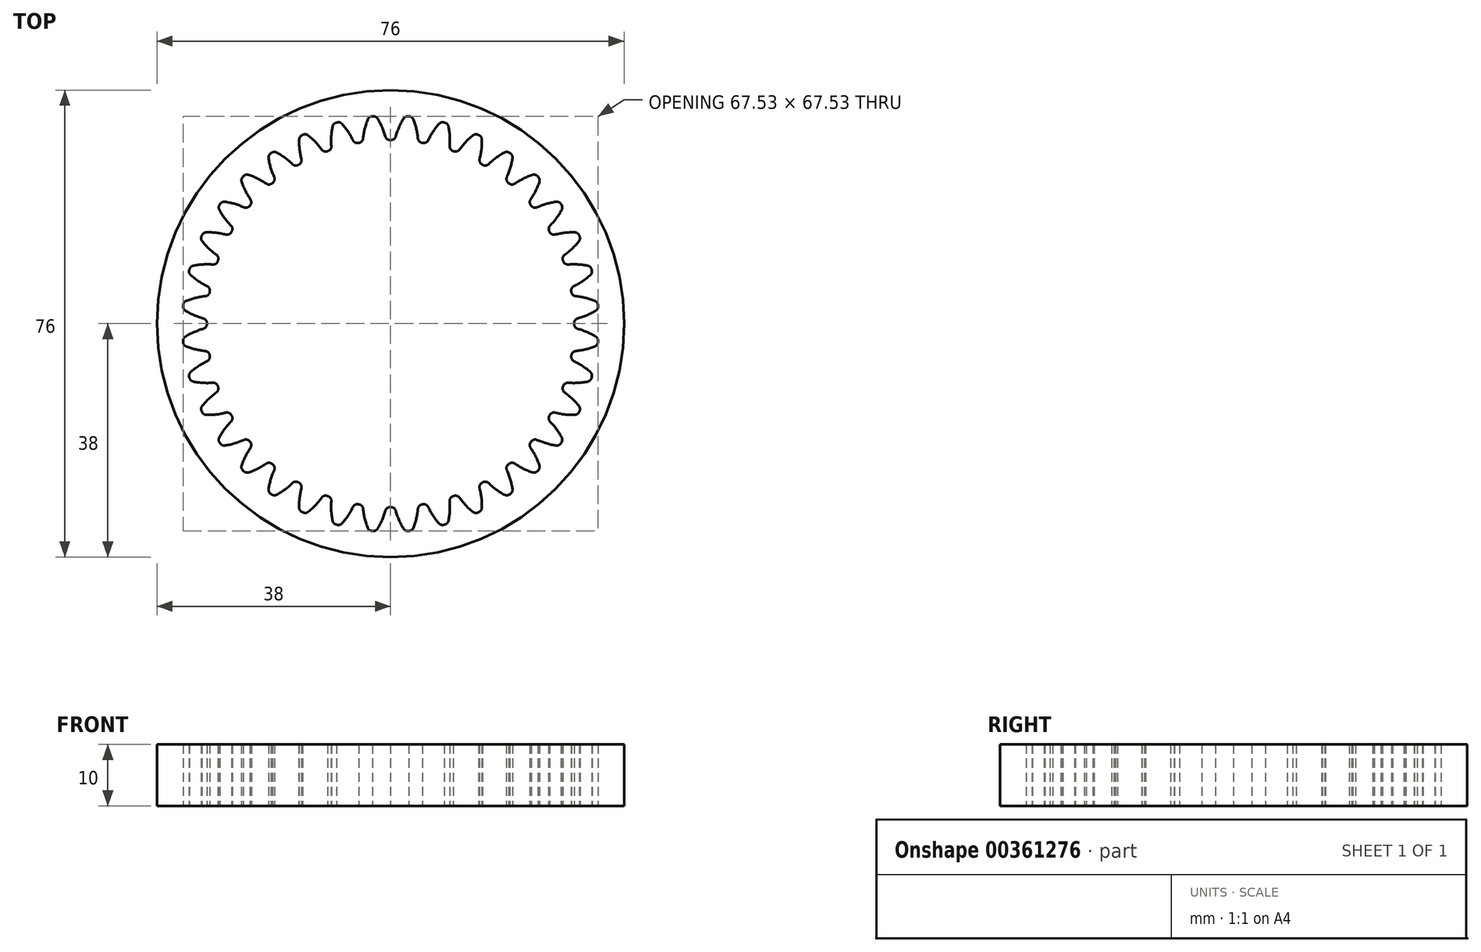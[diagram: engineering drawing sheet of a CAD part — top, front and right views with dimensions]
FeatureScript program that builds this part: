
annotation { "Feature Type Name" : "Feature", "Feature Type Description" : "" }
export const myFeature = defineFeature(function(context is Context, id is Id, definition is map)
    precondition{}
    {
        {
            var Q0;
            Q0=qCreatedBy(makeId("Top.planeOp"),FACE);
            var sketch = newSketch(context, id + "F0", { "sketchPlane" : qUnion([Q0])});
            skCircle(sketch, "E0", {"center": v(0, 0) * mm, "radius": 32.1 * mm, "construction": true});
            skCircle(sketch, "E1", {"center": v(0, 0) * mm, "radius": 33.88 * mm, "construction": true});
            skCircle(sketch, "E2", {"center": v(0, 0) * mm, "radius": 29.88 * mm, "construction": true});
            skLineSegment(sketch, "E3", {"start": v(0, 0) * mm, "end": v(0, 35.03) * mm, "construction": true});
            skLineSegment(sketch, "E4", {"start": v(0, 0) * mm, "end": v(-6.12, 34.73) * mm, "construction": true});
            skLineSegment(sketch, "E5", {"start": v(0, 0) * mm, "end": v(-3.06, 35) * mm, "construction": true});
            skCircle(sketch, "E6", {"center": v(-2.8, 31.98) * mm, "radius": 1.4 * mm, "construction": true});
            skPoint(sketch, "E7.center", {"position": v(0.05, 0.05) * mm});
            skCircle(sketch, "E8", {"center": v(0, 0) * mm, "radius": 38 * mm});
            skCircle(sketch, "E9", {"center": v(-2.8, 31.98) * mm, "radius": 10 * mm, "construction": true});
            skArc(sketch, "E10", {"start": v(-1.92, 21.9) * mm, "mid": v(-1.88, 21.97) * mm, "end": v(-1.85, 22.02) * mm});
            skArc(sketch, "E11.trimOffspring", {"start": v(-0.85, 30.47) * mm, "mid": v(-1.38, 31.97) * mm, "end": v(-2.11, 33.38) * mm});
            skLineSegment(sketch, "E12", {"start": v(-2.85, 33.76) * mm, "end": v(-2.95, 33.76) * mm});
            skLineSegment(sketch, "E13", {"start": v(-0.07, 29.88) * mm, "end": v(0, 29.88) * mm});
            skPoint(sketch, "E14.visualSharp", {"position": v(-0.7, 29.87) * mm});
            skArc(sketch, "E14.filletArc", {"start": v(-0.85, 30.47) * mm, "mid": v(-0.56, 30.04) * mm, "end": v(-0.07, 29.88) * mm});
            skPoint(sketch, "E15.visualSharp", {"position": v(-2.38, 33.8) * mm});
            skArc(sketch, "E15.filletArc", {"start": v(-2.11, 33.38) * mm, "mid": v(-2.43, 33.68) * mm, "end": v(-2.85, 33.76) * mm});
            skArc(sketch, "E16.MirrorCS", {"start": v(-4.46, 30.15) * mm, "mid": v(-4.67, 29.68) * mm, "end": v(-5.12, 29.44) * mm});
            skLineSegment(sketch, "E17.MirrorCS", {"start": v(-5.12, 29.44) * mm, "end": v(-5.19, 29.43) * mm});
            skArc(sketch, "E18.MirrorCS", {"start": v(-4.46, 30.15) * mm, "mid": v(-4.2, 31.72) * mm, "end": v(-3.72, 33.24) * mm});
            skArc(sketch, "E19.MirrorCS", {"start": v(-3.72, 33.24) * mm, "mid": v(-3.46, 33.59) * mm, "end": v(-3.06, 33.75) * mm});
            skLineSegment(sketch, "E20.MirrorCS", {"start": v(-3.06, 33.75) * mm, "end": v(-2.95, 33.76) * mm});
            skArc(sketch, "E21.1.0", {"start": v(-6.12, 29.86) * mm, "mid": v(-5.76, 29.49) * mm, "end": v(-5.25, 29.41) * mm});
            skLineSegment(sketch, "E21.1.1", {"start": v(-5.25, 29.41) * mm, "end": v(-5.19, 29.43) * mm});
            skArc(sketch, "E21.1.2", {"start": v(-6.12, 29.86) * mm, "mid": v(-6.9, 31.25) * mm, "end": v(-7.88, 32.51) * mm});
            skArc(sketch, "E21.1.3", {"start": v(-7.88, 32.51) * mm, "mid": v(-8.24, 32.74) * mm, "end": v(-8.67, 32.76) * mm});
            skLineSegment(sketch, "E21.1.4", {"start": v(-8.67, 32.76) * mm, "end": v(-8.77, 32.73) * mm});
            skLineSegment(sketch, "E21.1.5", {"start": v(-8.87, 32.7) * mm, "end": v(-8.77, 32.73) * mm});
            skArc(sketch, "E21.1.6", {"start": v(-9.43, 32.1) * mm, "mid": v(-9.24, 32.48) * mm, "end": v(-8.87, 32.7) * mm});
            skArc(sketch, "E21.1.7", {"start": v(-9.63, 28.92) * mm, "mid": v(-9.64, 30.51) * mm, "end": v(-9.43, 32.1) * mm});
            skArc(sketch, "E21.1.8", {"start": v(-9.63, 28.92) * mm, "mid": v(-9.75, 28.42) * mm, "end": v(-10.16, 28.1) * mm});
            skLineSegment(sketch, "E21.1.9", {"start": v(-10.16, 28.1) * mm, "end": v(-10.22, 28.08) * mm});
            skArc(sketch, "E21.2.0", {"start": v(-11.22, 28.34) * mm, "mid": v(-10.8, 28.04) * mm, "end": v(-10.28, 28.05) * mm});
            skLineSegment(sketch, "E21.2.1", {"start": v(-10.28, 28.05) * mm, "end": v(-10.22, 28.08) * mm});
            skArc(sketch, "E21.2.2", {"start": v(-11.22, 28.34) * mm, "mid": v(-12.23, 29.57) * mm, "end": v(-13.4, 30.65) * mm});
            skArc(sketch, "E21.2.3", {"start": v(-13.4, 30.65) * mm, "mid": v(-13.8, 30.82) * mm, "end": v(-14.22, 30.75) * mm});
            skLineSegment(sketch, "E21.2.4", {"start": v(-14.22, 30.75) * mm, "end": v(-14.32, 30.71) * mm});
            skLineSegment(sketch, "E21.2.5", {"start": v(-14.41, 30.66) * mm, "end": v(-14.32, 30.71) * mm});
            skArc(sketch, "E21.2.6", {"start": v(-14.86, 29.97) * mm, "mid": v(-14.74, 30.38) * mm, "end": v(-14.41, 30.66) * mm});
            skArc(sketch, "E21.2.7", {"start": v(-14.5, 26.8) * mm, "mid": v(-14.8, 28.37) * mm, "end": v(-14.86, 29.97) * mm});
            skArc(sketch, "E21.2.8", {"start": v(-14.5, 26.8) * mm, "mid": v(-14.54, 26.3) * mm, "end": v(-14.88, 25.9) * mm});
            skLineSegment(sketch, "E21.2.9", {"start": v(-14.88, 25.9) * mm, "end": v(-14.94, 25.88) * mm});
            skArc(sketch, "E21.3.0", {"start": v(-15.97, 25.96) * mm, "mid": v(-15.5, 25.74) * mm, "end": v(-15, 25.84) * mm});
            skLineSegment(sketch, "E21.3.1", {"start": v(-15, 25.84) * mm, "end": v(-14.94, 25.88) * mm});
            skArc(sketch, "E21.3.2", {"start": v(-15.97, 25.96) * mm, "mid": v(-17.18, 27) * mm, "end": v(-18.52, 27.86) * mm});
            skArc(sketch, "E21.3.3", {"start": v(-18.52, 27.86) * mm, "mid": v(-18.94, 27.95) * mm, "end": v(-19.35, 27.82) * mm});
            skLineSegment(sketch, "E21.3.4", {"start": v(-19.35, 27.82) * mm, "end": v(-19.44, 27.76) * mm});
            skLineSegment(sketch, "E21.3.5", {"start": v(-19.52, 27.7) * mm, "end": v(-19.44, 27.76) * mm});
            skArc(sketch, "E21.3.6", {"start": v(-19.84, 26.93) * mm, "mid": v(-19.79, 27.36) * mm, "end": v(-19.52, 27.7) * mm});
            skArc(sketch, "E21.3.7", {"start": v(-18.94, 23.88) * mm, "mid": v(-19.5, 25.37) * mm, "end": v(-19.84, 26.93) * mm});
            skArc(sketch, "E21.3.8", {"start": v(-18.94, 23.88) * mm, "mid": v(-18.88, 23.37) * mm, "end": v(-19.16, 22.93) * mm});
            skLineSegment(sketch, "E21.3.9", {"start": v(-19.16, 22.93) * mm, "end": v(-19.2, 22.89) * mm});
            skArc(sketch, "E21.4.0", {"start": v(-20.23, 22.8) * mm, "mid": v(-19.74, 22.65) * mm, "end": v(-19.26, 22.85) * mm});
            skLineSegment(sketch, "E21.4.1", {"start": v(-19.26, 22.85) * mm, "end": v(-19.2, 22.89) * mm});
            skArc(sketch, "E21.4.2", {"start": v(-20.23, 22.8) * mm, "mid": v(-21.6, 23.6) * mm, "end": v(-23.08, 24.22) * mm});
            skArc(sketch, "E21.4.3", {"start": v(-23.08, 24.22) * mm, "mid": v(-23.5, 24.24) * mm, "end": v(-23.88, 24.03) * mm});
            skLineSegment(sketch, "E21.4.4", {"start": v(-23.88, 24.03) * mm, "end": v(-23.96, 23.96) * mm});
            skLineSegment(sketch, "E21.4.5", {"start": v(-24.03, 23.88) * mm, "end": v(-23.96, 23.96) * mm});
            skArc(sketch, "E21.4.6", {"start": v(-24.22, 23.08) * mm, "mid": v(-24.24, 23.5) * mm, "end": v(-24.03, 23.88) * mm});
            skArc(sketch, "E21.4.7", {"start": v(-22.8, 20.23) * mm, "mid": v(-23.6, 21.6) * mm, "end": v(-24.22, 23.08) * mm});
            skArc(sketch, "E21.4.8", {"start": v(-22.8, 20.23) * mm, "mid": v(-22.65, 19.74) * mm, "end": v(-22.85, 19.26) * mm});
            skLineSegment(sketch, "E21.4.9", {"start": v(-22.85, 19.26) * mm, "end": v(-22.89, 19.2) * mm});
            skArc(sketch, "E21.5.0", {"start": v(-23.88, 18.94) * mm, "mid": v(-23.37, 18.88) * mm, "end": v(-22.93, 19.16) * mm});
            skLineSegment(sketch, "E21.5.1", {"start": v(-22.93, 19.16) * mm, "end": v(-22.89, 19.2) * mm});
            skArc(sketch, "E21.5.2", {"start": v(-23.88, 18.94) * mm, "mid": v(-25.37, 19.5) * mm, "end": v(-26.93, 19.84) * mm});
            skArc(sketch, "E21.5.3", {"start": v(-26.93, 19.84) * mm, "mid": v(-27.36, 19.79) * mm, "end": v(-27.7, 19.52) * mm});
            skLineSegment(sketch, "E21.5.4", {"start": v(-27.7, 19.52) * mm, "end": v(-27.76, 19.44) * mm});
            skLineSegment(sketch, "E21.5.5", {"start": v(-27.82, 19.35) * mm, "end": v(-27.76, 19.44) * mm});
            skArc(sketch, "E21.5.6", {"start": v(-27.86, 18.52) * mm, "mid": v(-27.95, 18.94) * mm, "end": v(-27.82, 19.35) * mm});
            skArc(sketch, "E21.5.7", {"start": v(-25.96, 15.97) * mm, "mid": v(-27, 17.18) * mm, "end": v(-27.86, 18.52) * mm});
            skArc(sketch, "E21.5.8", {"start": v(-25.96, 15.97) * mm, "mid": v(-25.74, 15.5) * mm, "end": v(-25.84, 15) * mm});
            skLineSegment(sketch, "E21.5.9", {"start": v(-25.84, 15) * mm, "end": v(-25.88, 14.94) * mm});
            skArc(sketch, "E21.6.0", {"start": v(-26.8, 14.5) * mm, "mid": v(-26.3, 14.54) * mm, "end": v(-25.9, 14.88) * mm});
            skLineSegment(sketch, "E21.6.1", {"start": v(-25.9, 14.88) * mm, "end": v(-25.88, 14.94) * mm});
            skArc(sketch, "E21.6.2", {"start": v(-26.8, 14.5) * mm, "mid": v(-28.37, 14.8) * mm, "end": v(-29.97, 14.86) * mm});
            skArc(sketch, "E21.6.3", {"start": v(-29.97, 14.86) * mm, "mid": v(-30.38, 14.74) * mm, "end": v(-30.66, 14.41) * mm});
            skLineSegment(sketch, "E21.6.4", {"start": v(-30.66, 14.41) * mm, "end": v(-30.71, 14.32) * mm});
            skLineSegment(sketch, "E21.6.5", {"start": v(-30.75, 14.22) * mm, "end": v(-30.71, 14.32) * mm});
            skArc(sketch, "E21.6.6", {"start": v(-30.65, 13.4) * mm, "mid": v(-30.82, 13.8) * mm, "end": v(-30.75, 14.22) * mm});
            skArc(sketch, "E21.6.7", {"start": v(-28.34, 11.22) * mm, "mid": v(-29.57, 12.23) * mm, "end": v(-30.65, 13.4) * mm});
            skArc(sketch, "E21.6.8", {"start": v(-28.34, 11.22) * mm, "mid": v(-28.04, 10.8) * mm, "end": v(-28.05, 10.28) * mm});
            skLineSegment(sketch, "E21.6.9", {"start": v(-28.05, 10.28) * mm, "end": v(-28.08, 10.22) * mm});
            skArc(sketch, "E21.7.0", {"start": v(-28.92, 9.63) * mm, "mid": v(-28.42, 9.75) * mm, "end": v(-28.1, 10.16) * mm});
            skLineSegment(sketch, "E21.7.1", {"start": v(-28.1, 10.16) * mm, "end": v(-28.08, 10.22) * mm});
            skArc(sketch, "E21.7.2", {"start": v(-28.92, 9.63) * mm, "mid": v(-30.51, 9.64) * mm, "end": v(-32.1, 9.43) * mm});
            skArc(sketch, "E21.7.3", {"start": v(-32.1, 9.43) * mm, "mid": v(-32.48, 9.24) * mm, "end": v(-32.7, 8.87) * mm});
            skLineSegment(sketch, "E21.7.4", {"start": v(-32.7, 8.87) * mm, "end": v(-32.73, 8.77) * mm});
            skLineSegment(sketch, "E21.7.5", {"start": v(-32.76, 8.67) * mm, "end": v(-32.73, 8.77) * mm});
            skArc(sketch, "E21.7.6", {"start": v(-32.51, 7.88) * mm, "mid": v(-32.74, 8.24) * mm, "end": v(-32.76, 8.67) * mm});
            skArc(sketch, "E21.7.7", {"start": v(-29.86, 6.12) * mm, "mid": v(-31.25, 6.9) * mm, "end": v(-32.51, 7.88) * mm});
            skArc(sketch, "E21.7.8", {"start": v(-29.86, 6.12) * mm, "mid": v(-29.49, 5.76) * mm, "end": v(-29.41, 5.25) * mm});
            skLineSegment(sketch, "E21.7.9", {"start": v(-29.41, 5.25) * mm, "end": v(-29.43, 5.19) * mm});
            skArc(sketch, "E21.8.0", {"start": v(-30.15, 4.46) * mm, "mid": v(-29.68, 4.67) * mm, "end": v(-29.44, 5.12) * mm});
            skLineSegment(sketch, "E21.8.1", {"start": v(-29.44, 5.12) * mm, "end": v(-29.43, 5.19) * mm});
            skArc(sketch, "E21.8.2", {"start": v(-30.15, 4.46) * mm, "mid": v(-31.72, 4.2) * mm, "end": v(-33.24, 3.72) * mm});
            skArc(sketch, "E21.8.3", {"start": v(-33.24, 3.72) * mm, "mid": v(-33.59, 3.46) * mm, "end": v(-33.75, 3.06) * mm});
            skLineSegment(sketch, "E21.8.4", {"start": v(-33.75, 3.06) * mm, "end": v(-33.76, 2.95) * mm});
            skLineSegment(sketch, "E21.8.5", {"start": v(-33.76, 2.85) * mm, "end": v(-33.76, 2.95) * mm});
            skArc(sketch, "E21.8.6", {"start": v(-33.38, 2.11) * mm, "mid": v(-33.68, 2.43) * mm, "end": v(-33.76, 2.85) * mm});
            skArc(sketch, "E21.8.7", {"start": v(-30.47, 0.85) * mm, "mid": v(-31.97, 1.38) * mm, "end": v(-33.38, 2.11) * mm});
            skArc(sketch, "E21.8.8", {"start": v(-30.47, 0.85) * mm, "mid": v(-30.04, 0.56) * mm, "end": v(-29.88, 0.07) * mm});
            skLineSegment(sketch, "E21.8.9", {"start": v(-29.88, 0.07) * mm, "end": v(-29.88, 0) * mm});
            skArc(sketch, "E21.9.0", {"start": v(-30.47, -0.85) * mm, "mid": v(-30.04, -0.56) * mm, "end": v(-29.88, -0.07) * mm});
            skLineSegment(sketch, "E21.9.1", {"start": v(-29.88, -0.07) * mm, "end": v(-29.88, 0) * mm});
            skArc(sketch, "E21.9.2", {"start": v(-30.47, -0.85) * mm, "mid": v(-31.97, -1.38) * mm, "end": v(-33.38, -2.11) * mm});
            skArc(sketch, "E21.9.3", {"start": v(-33.38, -2.11) * mm, "mid": v(-33.68, -2.43) * mm, "end": v(-33.76, -2.85) * mm});
            skLineSegment(sketch, "E21.9.4", {"start": v(-33.76, -2.85) * mm, "end": v(-33.76, -2.95) * mm});
            skLineSegment(sketch, "E21.9.5", {"start": v(-33.75, -3.06) * mm, "end": v(-33.76, -2.95) * mm});
            skArc(sketch, "E21.9.6", {"start": v(-33.24, -3.72) * mm, "mid": v(-33.59, -3.46) * mm, "end": v(-33.75, -3.06) * mm});
            skArc(sketch, "E21.9.7", {"start": v(-30.15, -4.46) * mm, "mid": v(-31.72, -4.2) * mm, "end": v(-33.24, -3.72) * mm});
            skArc(sketch, "E21.9.8", {"start": v(-30.15, -4.46) * mm, "mid": v(-29.68, -4.67) * mm, "end": v(-29.44, -5.12) * mm});
            skLineSegment(sketch, "E21.9.9", {"start": v(-29.44, -5.12) * mm, "end": v(-29.43, -5.19) * mm});
            skArc(sketch, "E21.10.0", {"start": v(-29.86, -6.12) * mm, "mid": v(-29.49, -5.76) * mm, "end": v(-29.41, -5.25) * mm});
            skLineSegment(sketch, "E21.10.1", {"start": v(-29.41, -5.25) * mm, "end": v(-29.43, -5.19) * mm});
            skArc(sketch, "E21.10.2", {"start": v(-29.86, -6.12) * mm, "mid": v(-31.25, -6.9) * mm, "end": v(-32.51, -7.88) * mm});
            skArc(sketch, "E21.10.3", {"start": v(-32.51, -7.88) * mm, "mid": v(-32.74, -8.24) * mm, "end": v(-32.76, -8.67) * mm});
            skLineSegment(sketch, "E21.10.4", {"start": v(-32.76, -8.67) * mm, "end": v(-32.73, -8.77) * mm});
            skLineSegment(sketch, "E21.10.5", {"start": v(-32.7, -8.87) * mm, "end": v(-32.73, -8.77) * mm});
            skArc(sketch, "E21.10.6", {"start": v(-32.1, -9.43) * mm, "mid": v(-32.48, -9.24) * mm, "end": v(-32.7, -8.87) * mm});
            skArc(sketch, "E21.10.7", {"start": v(-28.92, -9.63) * mm, "mid": v(-30.51, -9.64) * mm, "end": v(-32.1, -9.43) * mm});
            skArc(sketch, "E21.10.8", {"start": v(-28.92, -9.63) * mm, "mid": v(-28.42, -9.75) * mm, "end": v(-28.1, -10.16) * mm});
            skLineSegment(sketch, "E21.10.9", {"start": v(-28.1, -10.16) * mm, "end": v(-28.08, -10.22) * mm});
            skArc(sketch, "E21.11.0", {"start": v(-28.34, -11.22) * mm, "mid": v(-28.04, -10.8) * mm, "end": v(-28.05, -10.28) * mm});
            skLineSegment(sketch, "E21.11.1", {"start": v(-28.05, -10.28) * mm, "end": v(-28.08, -10.22) * mm});
            skArc(sketch, "E21.11.2", {"start": v(-28.34, -11.22) * mm, "mid": v(-29.57, -12.23) * mm, "end": v(-30.65, -13.4) * mm});
            skArc(sketch, "E21.11.3", {"start": v(-30.65, -13.4) * mm, "mid": v(-30.82, -13.8) * mm, "end": v(-30.75, -14.22) * mm});
            skLineSegment(sketch, "E21.11.4", {"start": v(-30.75, -14.22) * mm, "end": v(-30.71, -14.32) * mm});
            skLineSegment(sketch, "E21.11.5", {"start": v(-30.66, -14.41) * mm, "end": v(-30.71, -14.32) * mm});
            skArc(sketch, "E21.11.6", {"start": v(-29.97, -14.86) * mm, "mid": v(-30.38, -14.74) * mm, "end": v(-30.66, -14.41) * mm});
            skArc(sketch, "E21.11.7", {"start": v(-26.8, -14.5) * mm, "mid": v(-28.37, -14.8) * mm, "end": v(-29.97, -14.86) * mm});
            skArc(sketch, "E21.11.8", {"start": v(-26.8, -14.5) * mm, "mid": v(-26.3, -14.54) * mm, "end": v(-25.9, -14.88) * mm});
            skLineSegment(sketch, "E21.11.9", {"start": v(-25.9, -14.88) * mm, "end": v(-25.88, -14.94) * mm});
            skArc(sketch, "E21.12.0", {"start": v(-25.96, -15.97) * mm, "mid": v(-25.74, -15.5) * mm, "end": v(-25.84, -15) * mm});
            skLineSegment(sketch, "E21.12.1", {"start": v(-25.84, -15) * mm, "end": v(-25.88, -14.94) * mm});
            skArc(sketch, "E21.12.2", {"start": v(-25.96, -15.97) * mm, "mid": v(-27, -17.18) * mm, "end": v(-27.86, -18.52) * mm});
            skArc(sketch, "E21.12.3", {"start": v(-27.86, -18.52) * mm, "mid": v(-27.95, -18.94) * mm, "end": v(-27.82, -19.35) * mm});
            skLineSegment(sketch, "E21.12.4", {"start": v(-27.82, -19.35) * mm, "end": v(-27.76, -19.44) * mm});
            skLineSegment(sketch, "E21.12.5", {"start": v(-27.7, -19.52) * mm, "end": v(-27.76, -19.44) * mm});
            skArc(sketch, "E21.12.6", {"start": v(-26.93, -19.84) * mm, "mid": v(-27.36, -19.79) * mm, "end": v(-27.7, -19.52) * mm});
            skArc(sketch, "E21.12.7", {"start": v(-23.88, -18.94) * mm, "mid": v(-25.37, -19.5) * mm, "end": v(-26.93, -19.84) * mm});
            skArc(sketch, "E21.12.8", {"start": v(-23.88, -18.94) * mm, "mid": v(-23.37, -18.88) * mm, "end": v(-22.93, -19.16) * mm});
            skLineSegment(sketch, "E21.12.9", {"start": v(-22.93, -19.16) * mm, "end": v(-22.89, -19.2) * mm});
            skArc(sketch, "E21.13.0", {"start": v(-22.8, -20.23) * mm, "mid": v(-22.65, -19.74) * mm, "end": v(-22.85, -19.26) * mm});
            skLineSegment(sketch, "E21.13.1", {"start": v(-22.85, -19.26) * mm, "end": v(-22.89, -19.2) * mm});
            skArc(sketch, "E21.13.2", {"start": v(-22.8, -20.23) * mm, "mid": v(-23.6, -21.6) * mm, "end": v(-24.22, -23.08) * mm});
            skArc(sketch, "E21.13.3", {"start": v(-24.22, -23.08) * mm, "mid": v(-24.24, -23.5) * mm, "end": v(-24.03, -23.88) * mm});
            skLineSegment(sketch, "E21.13.4", {"start": v(-24.03, -23.88) * mm, "end": v(-23.96, -23.96) * mm});
            skLineSegment(sketch, "E21.13.5", {"start": v(-23.88, -24.03) * mm, "end": v(-23.96, -23.96) * mm});
            skArc(sketch, "E21.13.6", {"start": v(-23.08, -24.22) * mm, "mid": v(-23.5, -24.24) * mm, "end": v(-23.88, -24.03) * mm});
            skArc(sketch, "E21.13.7", {"start": v(-20.23, -22.8) * mm, "mid": v(-21.6, -23.6) * mm, "end": v(-23.08, -24.22) * mm});
            skArc(sketch, "E21.13.8", {"start": v(-20.23, -22.8) * mm, "mid": v(-19.74, -22.65) * mm, "end": v(-19.26, -22.85) * mm});
            skLineSegment(sketch, "E21.13.9", {"start": v(-19.26, -22.85) * mm, "end": v(-19.2, -22.89) * mm});
            skArc(sketch, "E21.14.0", {"start": v(-18.94, -23.88) * mm, "mid": v(-18.88, -23.37) * mm, "end": v(-19.16, -22.93) * mm});
            skLineSegment(sketch, "E21.14.1", {"start": v(-19.16, -22.93) * mm, "end": v(-19.2, -22.89) * mm});
            skArc(sketch, "E21.14.2", {"start": v(-18.94, -23.88) * mm, "mid": v(-19.5, -25.37) * mm, "end": v(-19.84, -26.93) * mm});
            skArc(sketch, "E21.14.3", {"start": v(-19.84, -26.93) * mm, "mid": v(-19.79, -27.36) * mm, "end": v(-19.52, -27.7) * mm});
            skLineSegment(sketch, "E21.14.4", {"start": v(-19.52, -27.7) * mm, "end": v(-19.44, -27.76) * mm});
            skLineSegment(sketch, "E21.14.5", {"start": v(-19.35, -27.82) * mm, "end": v(-19.44, -27.76) * mm});
            skArc(sketch, "E21.14.6", {"start": v(-18.52, -27.86) * mm, "mid": v(-18.94, -27.95) * mm, "end": v(-19.35, -27.82) * mm});
            skArc(sketch, "E21.14.7", {"start": v(-15.97, -25.96) * mm, "mid": v(-17.18, -27) * mm, "end": v(-18.52, -27.86) * mm});
            skArc(sketch, "E21.14.8", {"start": v(-15.97, -25.96) * mm, "mid": v(-15.5, -25.74) * mm, "end": v(-15, -25.84) * mm});
            skLineSegment(sketch, "E21.14.9", {"start": v(-15, -25.84) * mm, "end": v(-14.94, -25.88) * mm});
            skArc(sketch, "E21.15.0", {"start": v(-14.5, -26.8) * mm, "mid": v(-14.54, -26.3) * mm, "end": v(-14.88, -25.9) * mm});
            skLineSegment(sketch, "E21.15.1", {"start": v(-14.88, -25.9) * mm, "end": v(-14.94, -25.88) * mm});
            skArc(sketch, "E21.15.2", {"start": v(-14.5, -26.8) * mm, "mid": v(-14.8, -28.37) * mm, "end": v(-14.86, -29.97) * mm});
            skArc(sketch, "E21.15.3", {"start": v(-14.86, -29.97) * mm, "mid": v(-14.74, -30.38) * mm, "end": v(-14.41, -30.66) * mm});
            skLineSegment(sketch, "E21.15.4", {"start": v(-14.41, -30.66) * mm, "end": v(-14.32, -30.71) * mm});
            skLineSegment(sketch, "E21.15.5", {"start": v(-14.22, -30.75) * mm, "end": v(-14.32, -30.71) * mm});
            skArc(sketch, "E21.15.6", {"start": v(-13.4, -30.65) * mm, "mid": v(-13.8, -30.82) * mm, "end": v(-14.22, -30.75) * mm});
            skArc(sketch, "E21.15.7", {"start": v(-11.22, -28.34) * mm, "mid": v(-12.23, -29.57) * mm, "end": v(-13.4, -30.65) * mm});
            skArc(sketch, "E21.15.8", {"start": v(-11.22, -28.34) * mm, "mid": v(-10.8, -28.04) * mm, "end": v(-10.28, -28.05) * mm});
            skLineSegment(sketch, "E21.15.9", {"start": v(-10.28, -28.05) * mm, "end": v(-10.22, -28.08) * mm});
            skArc(sketch, "E21.16.0", {"start": v(-9.63, -28.92) * mm, "mid": v(-9.75, -28.42) * mm, "end": v(-10.16, -28.1) * mm});
            skLineSegment(sketch, "E21.16.1", {"start": v(-10.16, -28.1) * mm, "end": v(-10.22, -28.08) * mm});
            skArc(sketch, "E21.16.2", {"start": v(-9.63, -28.92) * mm, "mid": v(-9.64, -30.51) * mm, "end": v(-9.43, -32.1) * mm});
            skArc(sketch, "E21.16.3", {"start": v(-9.43, -32.1) * mm, "mid": v(-9.24, -32.48) * mm, "end": v(-8.87, -32.7) * mm});
            skLineSegment(sketch, "E21.16.4", {"start": v(-8.87, -32.7) * mm, "end": v(-8.77, -32.73) * mm});
            skLineSegment(sketch, "E21.16.5", {"start": v(-8.67, -32.76) * mm, "end": v(-8.77, -32.73) * mm});
            skArc(sketch, "E21.16.6", {"start": v(-7.88, -32.51) * mm, "mid": v(-8.24, -32.74) * mm, "end": v(-8.67, -32.76) * mm});
            skArc(sketch, "E21.16.7", {"start": v(-6.12, -29.86) * mm, "mid": v(-6.9, -31.25) * mm, "end": v(-7.88, -32.51) * mm});
            skArc(sketch, "E21.16.8", {"start": v(-6.12, -29.86) * mm, "mid": v(-5.76, -29.49) * mm, "end": v(-5.25, -29.41) * mm});
            skLineSegment(sketch, "E21.16.9", {"start": v(-5.25, -29.41) * mm, "end": v(-5.19, -29.43) * mm});
            skArc(sketch, "E21.17.0", {"start": v(-4.46, -30.15) * mm, "mid": v(-4.67, -29.68) * mm, "end": v(-5.12, -29.44) * mm});
            skLineSegment(sketch, "E21.17.1", {"start": v(-5.12, -29.44) * mm, "end": v(-5.19, -29.43) * mm});
            skArc(sketch, "E21.17.2", {"start": v(-4.46, -30.15) * mm, "mid": v(-4.2, -31.72) * mm, "end": v(-3.72, -33.24) * mm});
            skArc(sketch, "E21.17.3", {"start": v(-3.72, -33.24) * mm, "mid": v(-3.46, -33.59) * mm, "end": v(-3.06, -33.75) * mm});
            skLineSegment(sketch, "E21.17.4", {"start": v(-3.06, -33.75) * mm, "end": v(-2.95, -33.76) * mm});
            skLineSegment(sketch, "E21.17.5", {"start": v(-2.85, -33.76) * mm, "end": v(-2.95, -33.76) * mm});
            skArc(sketch, "E21.17.6", {"start": v(-2.11, -33.38) * mm, "mid": v(-2.43, -33.68) * mm, "end": v(-2.85, -33.76) * mm});
            skArc(sketch, "E21.17.7", {"start": v(-0.85, -30.47) * mm, "mid": v(-1.38, -31.97) * mm, "end": v(-2.11, -33.38) * mm});
            skArc(sketch, "E21.17.8", {"start": v(-0.85, -30.47) * mm, "mid": v(-0.56, -30.04) * mm, "end": v(-0.07, -29.88) * mm});
            skLineSegment(sketch, "E21.17.9", {"start": v(-0.07, -29.88) * mm, "end": v(0, -29.88) * mm});
            skArc(sketch, "E21.18.0", {"start": v(0.85, -30.47) * mm, "mid": v(0.56, -30.04) * mm, "end": v(0.07, -29.88) * mm});
            skLineSegment(sketch, "E21.18.1", {"start": v(0.07, -29.88) * mm, "end": v(0, -29.88) * mm});
            skArc(sketch, "E21.18.2", {"start": v(0.85, -30.47) * mm, "mid": v(1.38, -31.97) * mm, "end": v(2.11, -33.38) * mm});
            skArc(sketch, "E21.18.3", {"start": v(2.11, -33.38) * mm, "mid": v(2.43, -33.68) * mm, "end": v(2.85, -33.76) * mm});
            skLineSegment(sketch, "E21.18.4", {"start": v(2.85, -33.76) * mm, "end": v(2.95, -33.76) * mm});
            skLineSegment(sketch, "E21.18.5", {"start": v(3.06, -33.75) * mm, "end": v(2.95, -33.76) * mm});
            skArc(sketch, "E21.18.6", {"start": v(3.72, -33.24) * mm, "mid": v(3.46, -33.59) * mm, "end": v(3.06, -33.75) * mm});
            skArc(sketch, "E21.18.7", {"start": v(4.46, -30.15) * mm, "mid": v(4.2, -31.72) * mm, "end": v(3.72, -33.24) * mm});
            skArc(sketch, "E21.18.8", {"start": v(4.46, -30.15) * mm, "mid": v(4.67, -29.68) * mm, "end": v(5.12, -29.44) * mm});
            skLineSegment(sketch, "E21.18.9", {"start": v(5.12, -29.44) * mm, "end": v(5.19, -29.43) * mm});
            skArc(sketch, "E21.19.0", {"start": v(6.12, -29.86) * mm, "mid": v(5.76, -29.49) * mm, "end": v(5.25, -29.41) * mm});
            skLineSegment(sketch, "E21.19.1", {"start": v(5.25, -29.41) * mm, "end": v(5.19, -29.43) * mm});
            skArc(sketch, "E21.19.2", {"start": v(6.12, -29.86) * mm, "mid": v(6.9, -31.25) * mm, "end": v(7.88, -32.51) * mm});
            skArc(sketch, "E21.19.3", {"start": v(7.88, -32.51) * mm, "mid": v(8.24, -32.74) * mm, "end": v(8.67, -32.76) * mm});
            skLineSegment(sketch, "E21.19.4", {"start": v(8.67, -32.76) * mm, "end": v(8.77, -32.73) * mm});
            skLineSegment(sketch, "E21.19.5", {"start": v(8.87, -32.7) * mm, "end": v(8.77, -32.73) * mm});
            skArc(sketch, "E21.19.6", {"start": v(9.43, -32.1) * mm, "mid": v(9.24, -32.48) * mm, "end": v(8.87, -32.7) * mm});
            skArc(sketch, "E21.19.7", {"start": v(9.63, -28.92) * mm, "mid": v(9.64, -30.51) * mm, "end": v(9.43, -32.1) * mm});
            skArc(sketch, "E21.19.8", {"start": v(9.63, -28.92) * mm, "mid": v(9.75, -28.42) * mm, "end": v(10.16, -28.1) * mm});
            skLineSegment(sketch, "E21.19.9", {"start": v(10.16, -28.1) * mm, "end": v(10.22, -28.08) * mm});
            skArc(sketch, "E21.20.0", {"start": v(11.22, -28.34) * mm, "mid": v(10.8, -28.04) * mm, "end": v(10.28, -28.05) * mm});
            skLineSegment(sketch, "E21.20.1", {"start": v(10.28, -28.05) * mm, "end": v(10.22, -28.08) * mm});
            skArc(sketch, "E21.20.2", {"start": v(11.22, -28.34) * mm, "mid": v(12.23, -29.57) * mm, "end": v(13.4, -30.65) * mm});
            skArc(sketch, "E21.20.3", {"start": v(13.4, -30.65) * mm, "mid": v(13.8, -30.82) * mm, "end": v(14.22, -30.75) * mm});
            skLineSegment(sketch, "E21.20.4", {"start": v(14.22, -30.75) * mm, "end": v(14.32, -30.71) * mm});
            skLineSegment(sketch, "E21.20.5", {"start": v(14.41, -30.66) * mm, "end": v(14.32, -30.71) * mm});
            skArc(sketch, "E21.20.6", {"start": v(14.86, -29.97) * mm, "mid": v(14.74, -30.38) * mm, "end": v(14.41, -30.66) * mm});
            skArc(sketch, "E21.20.7", {"start": v(14.5, -26.8) * mm, "mid": v(14.8, -28.37) * mm, "end": v(14.86, -29.97) * mm});
            skArc(sketch, "E21.20.8", {"start": v(14.5, -26.8) * mm, "mid": v(14.54, -26.3) * mm, "end": v(14.88, -25.9) * mm});
            skLineSegment(sketch, "E21.20.9", {"start": v(14.88, -25.9) * mm, "end": v(14.94, -25.88) * mm});
            skArc(sketch, "E21.21.0", {"start": v(15.97, -25.96) * mm, "mid": v(15.5, -25.74) * mm, "end": v(15, -25.84) * mm});
            skLineSegment(sketch, "E21.21.1", {"start": v(15, -25.84) * mm, "end": v(14.94, -25.88) * mm});
            skArc(sketch, "E21.21.2", {"start": v(15.97, -25.96) * mm, "mid": v(17.18, -27) * mm, "end": v(18.52, -27.86) * mm});
            skArc(sketch, "E21.21.3", {"start": v(18.52, -27.86) * mm, "mid": v(18.94, -27.95) * mm, "end": v(19.35, -27.82) * mm});
            skLineSegment(sketch, "E21.21.4", {"start": v(19.35, -27.82) * mm, "end": v(19.44, -27.76) * mm});
            skLineSegment(sketch, "E21.21.5", {"start": v(19.52, -27.7) * mm, "end": v(19.44, -27.76) * mm});
            skArc(sketch, "E21.21.6", {"start": v(19.84, -26.93) * mm, "mid": v(19.79, -27.36) * mm, "end": v(19.52, -27.7) * mm});
            skArc(sketch, "E21.21.7", {"start": v(18.94, -23.88) * mm, "mid": v(19.5, -25.37) * mm, "end": v(19.84, -26.93) * mm});
            skArc(sketch, "E21.21.8", {"start": v(18.94, -23.88) * mm, "mid": v(18.88, -23.37) * mm, "end": v(19.16, -22.93) * mm});
            skLineSegment(sketch, "E21.21.9", {"start": v(19.16, -22.93) * mm, "end": v(19.2, -22.89) * mm});
            skArc(sketch, "E21.22.0", {"start": v(20.23, -22.8) * mm, "mid": v(19.74, -22.65) * mm, "end": v(19.26, -22.85) * mm});
            skLineSegment(sketch, "E21.22.1", {"start": v(19.26, -22.85) * mm, "end": v(19.2, -22.89) * mm});
            skArc(sketch, "E21.22.2", {"start": v(20.23, -22.8) * mm, "mid": v(21.6, -23.6) * mm, "end": v(23.08, -24.22) * mm});
            skArc(sketch, "E21.22.3", {"start": v(23.08, -24.22) * mm, "mid": v(23.5, -24.24) * mm, "end": v(23.88, -24.03) * mm});
            skLineSegment(sketch, "E21.22.4", {"start": v(23.88, -24.03) * mm, "end": v(23.96, -23.96) * mm});
            skLineSegment(sketch, "E21.22.5", {"start": v(24.03, -23.88) * mm, "end": v(23.96, -23.96) * mm});
            skArc(sketch, "E21.22.6", {"start": v(24.22, -23.08) * mm, "mid": v(24.24, -23.5) * mm, "end": v(24.03, -23.88) * mm});
            skArc(sketch, "E21.22.7", {"start": v(22.8, -20.23) * mm, "mid": v(23.6, -21.6) * mm, "end": v(24.22, -23.08) * mm});
            skArc(sketch, "E21.22.8", {"start": v(22.8, -20.23) * mm, "mid": v(22.65, -19.74) * mm, "end": v(22.85, -19.26) * mm});
            skLineSegment(sketch, "E21.22.9", {"start": v(22.85, -19.26) * mm, "end": v(22.89, -19.2) * mm});
            skArc(sketch, "E21.23.0", {"start": v(23.88, -18.94) * mm, "mid": v(23.37, -18.88) * mm, "end": v(22.93, -19.16) * mm});
            skLineSegment(sketch, "E21.23.1", {"start": v(22.93, -19.16) * mm, "end": v(22.89, -19.2) * mm});
            skArc(sketch, "E21.23.2", {"start": v(23.88, -18.94) * mm, "mid": v(25.37, -19.5) * mm, "end": v(26.93, -19.84) * mm});
            skArc(sketch, "E21.23.3", {"start": v(26.93, -19.84) * mm, "mid": v(27.36, -19.79) * mm, "end": v(27.7, -19.52) * mm});
            skLineSegment(sketch, "E21.23.4", {"start": v(27.7, -19.52) * mm, "end": v(27.76, -19.44) * mm});
            skLineSegment(sketch, "E21.23.5", {"start": v(27.82, -19.35) * mm, "end": v(27.76, -19.44) * mm});
            skArc(sketch, "E21.23.6", {"start": v(27.86, -18.52) * mm, "mid": v(27.95, -18.94) * mm, "end": v(27.82, -19.35) * mm});
            skArc(sketch, "E21.23.7", {"start": v(25.96, -15.97) * mm, "mid": v(27, -17.18) * mm, "end": v(27.86, -18.52) * mm});
            skArc(sketch, "E21.23.8", {"start": v(25.96, -15.97) * mm, "mid": v(25.74, -15.5) * mm, "end": v(25.84, -15) * mm});
            skLineSegment(sketch, "E21.23.9", {"start": v(25.84, -15) * mm, "end": v(25.88, -14.94) * mm});
            skArc(sketch, "E21.24.0", {"start": v(26.8, -14.5) * mm, "mid": v(26.3, -14.54) * mm, "end": v(25.9, -14.88) * mm});
            skLineSegment(sketch, "E21.24.1", {"start": v(25.9, -14.88) * mm, "end": v(25.88, -14.94) * mm});
            skArc(sketch, "E21.24.2", {"start": v(26.8, -14.5) * mm, "mid": v(28.37, -14.8) * mm, "end": v(29.97, -14.86) * mm});
            skArc(sketch, "E21.24.3", {"start": v(29.97, -14.86) * mm, "mid": v(30.38, -14.74) * mm, "end": v(30.66, -14.41) * mm});
            skLineSegment(sketch, "E21.24.4", {"start": v(30.66, -14.41) * mm, "end": v(30.71, -14.32) * mm});
            skLineSegment(sketch, "E21.24.5", {"start": v(30.75, -14.22) * mm, "end": v(30.71, -14.32) * mm});
            skArc(sketch, "E21.24.6", {"start": v(30.65, -13.4) * mm, "mid": v(30.82, -13.8) * mm, "end": v(30.75, -14.22) * mm});
            skArc(sketch, "E21.24.7", {"start": v(28.34, -11.22) * mm, "mid": v(29.57, -12.23) * mm, "end": v(30.65, -13.4) * mm});
            skArc(sketch, "E21.24.8", {"start": v(28.34, -11.22) * mm, "mid": v(28.04, -10.8) * mm, "end": v(28.05, -10.28) * mm});
            skLineSegment(sketch, "E21.24.9", {"start": v(28.05, -10.28) * mm, "end": v(28.08, -10.22) * mm});
            skArc(sketch, "E21.25.0", {"start": v(28.92, -9.63) * mm, "mid": v(28.42, -9.75) * mm, "end": v(28.1, -10.16) * mm});
            skLineSegment(sketch, "E21.25.1", {"start": v(28.1, -10.16) * mm, "end": v(28.08, -10.22) * mm});
            skArc(sketch, "E21.25.2", {"start": v(28.92, -9.63) * mm, "mid": v(30.51, -9.64) * mm, "end": v(32.1, -9.43) * mm});
            skArc(sketch, "E21.25.3", {"start": v(32.1, -9.43) * mm, "mid": v(32.48, -9.24) * mm, "end": v(32.7, -8.87) * mm});
            skLineSegment(sketch, "E21.25.4", {"start": v(32.7, -8.87) * mm, "end": v(32.73, -8.77) * mm});
            skLineSegment(sketch, "E21.25.5", {"start": v(32.76, -8.67) * mm, "end": v(32.73, -8.77) * mm});
            skArc(sketch, "E21.25.6", {"start": v(32.51, -7.88) * mm, "mid": v(32.74, -8.24) * mm, "end": v(32.76, -8.67) * mm});
            skArc(sketch, "E21.25.7", {"start": v(29.86, -6.12) * mm, "mid": v(31.25, -6.9) * mm, "end": v(32.51, -7.88) * mm});
            skArc(sketch, "E21.25.8", {"start": v(29.86, -6.12) * mm, "mid": v(29.49, -5.76) * mm, "end": v(29.41, -5.25) * mm});
            skLineSegment(sketch, "E21.25.9", {"start": v(29.41, -5.25) * mm, "end": v(29.43, -5.19) * mm});
            skArc(sketch, "E21.26.0", {"start": v(30.15, -4.46) * mm, "mid": v(29.68, -4.67) * mm, "end": v(29.44, -5.12) * mm});
            skLineSegment(sketch, "E21.26.1", {"start": v(29.44, -5.12) * mm, "end": v(29.43, -5.19) * mm});
            skArc(sketch, "E21.26.2", {"start": v(30.15, -4.46) * mm, "mid": v(31.72, -4.2) * mm, "end": v(33.24, -3.72) * mm});
            skArc(sketch, "E21.26.3", {"start": v(33.24, -3.72) * mm, "mid": v(33.59, -3.46) * mm, "end": v(33.75, -3.06) * mm});
            skLineSegment(sketch, "E21.26.4", {"start": v(33.75, -3.06) * mm, "end": v(33.76, -2.95) * mm});
            skLineSegment(sketch, "E21.26.5", {"start": v(33.76, -2.85) * mm, "end": v(33.76, -2.95) * mm});
            skArc(sketch, "E21.26.6", {"start": v(33.38, -2.11) * mm, "mid": v(33.68, -2.43) * mm, "end": v(33.76, -2.85) * mm});
            skArc(sketch, "E21.26.7", {"start": v(30.47, -0.85) * mm, "mid": v(31.97, -1.38) * mm, "end": v(33.38, -2.11) * mm});
            skArc(sketch, "E21.26.8", {"start": v(30.47, -0.85) * mm, "mid": v(30.04, -0.56) * mm, "end": v(29.88, -0.07) * mm});
            skLineSegment(sketch, "E21.26.9", {"start": v(29.88, -0.07) * mm, "end": v(29.88, 0) * mm});
            skArc(sketch, "E21.27.0", {"start": v(30.47, 0.85) * mm, "mid": v(30.04, 0.56) * mm, "end": v(29.88, 0.07) * mm});
            skLineSegment(sketch, "E21.27.1", {"start": v(29.88, 0.07) * mm, "end": v(29.88, 0) * mm});
            skArc(sketch, "E21.27.2", {"start": v(30.47, 0.85) * mm, "mid": v(31.97, 1.38) * mm, "end": v(33.38, 2.11) * mm});
            skArc(sketch, "E21.27.3", {"start": v(33.38, 2.11) * mm, "mid": v(33.68, 2.43) * mm, "end": v(33.76, 2.85) * mm});
            skLineSegment(sketch, "E21.27.4", {"start": v(33.76, 2.85) * mm, "end": v(33.76, 2.95) * mm});
            skLineSegment(sketch, "E21.27.5", {"start": v(33.75, 3.06) * mm, "end": v(33.76, 2.95) * mm});
            skArc(sketch, "E21.27.6", {"start": v(33.24, 3.72) * mm, "mid": v(33.59, 3.46) * mm, "end": v(33.75, 3.06) * mm});
            skArc(sketch, "E21.27.7", {"start": v(30.15, 4.46) * mm, "mid": v(31.72, 4.2) * mm, "end": v(33.24, 3.72) * mm});
            skArc(sketch, "E21.27.8", {"start": v(30.15, 4.46) * mm, "mid": v(29.68, 4.67) * mm, "end": v(29.44, 5.12) * mm});
            skLineSegment(sketch, "E21.27.9", {"start": v(29.44, 5.12) * mm, "end": v(29.43, 5.19) * mm});
            skArc(sketch, "E21.28.0", {"start": v(29.86, 6.12) * mm, "mid": v(29.49, 5.76) * mm, "end": v(29.41, 5.25) * mm});
            skLineSegment(sketch, "E21.28.1", {"start": v(29.41, 5.25) * mm, "end": v(29.43, 5.19) * mm});
            skArc(sketch, "E21.28.2", {"start": v(29.86, 6.12) * mm, "mid": v(31.25, 6.9) * mm, "end": v(32.51, 7.88) * mm});
            skArc(sketch, "E21.28.3", {"start": v(32.51, 7.88) * mm, "mid": v(32.74, 8.24) * mm, "end": v(32.76, 8.67) * mm});
            skLineSegment(sketch, "E21.28.4", {"start": v(32.76, 8.67) * mm, "end": v(32.73, 8.77) * mm});
            skLineSegment(sketch, "E21.28.5", {"start": v(32.7, 8.87) * mm, "end": v(32.73, 8.77) * mm});
            skArc(sketch, "E21.28.6", {"start": v(32.1, 9.43) * mm, "mid": v(32.48, 9.24) * mm, "end": v(32.7, 8.87) * mm});
            skArc(sketch, "E21.28.7", {"start": v(28.92, 9.63) * mm, "mid": v(30.51, 9.64) * mm, "end": v(32.1, 9.43) * mm});
            skArc(sketch, "E21.28.8", {"start": v(28.92, 9.63) * mm, "mid": v(28.42, 9.75) * mm, "end": v(28.1, 10.16) * mm});
            skLineSegment(sketch, "E21.28.9", {"start": v(28.1, 10.16) * mm, "end": v(28.08, 10.22) * mm});
            skArc(sketch, "E21.29.0", {"start": v(28.34, 11.22) * mm, "mid": v(28.04, 10.8) * mm, "end": v(28.05, 10.28) * mm});
            skLineSegment(sketch, "E21.29.1", {"start": v(28.05, 10.28) * mm, "end": v(28.08, 10.22) * mm});
            skArc(sketch, "E21.29.2", {"start": v(28.34, 11.22) * mm, "mid": v(29.57, 12.23) * mm, "end": v(30.65, 13.4) * mm});
            skArc(sketch, "E21.29.3", {"start": v(30.65, 13.4) * mm, "mid": v(30.82, 13.8) * mm, "end": v(30.75, 14.22) * mm});
            skLineSegment(sketch, "E21.29.4", {"start": v(30.75, 14.22) * mm, "end": v(30.71, 14.32) * mm});
            skLineSegment(sketch, "E21.29.5", {"start": v(30.66, 14.41) * mm, "end": v(30.71, 14.32) * mm});
            skArc(sketch, "E21.29.6", {"start": v(29.97, 14.86) * mm, "mid": v(30.38, 14.74) * mm, "end": v(30.66, 14.41) * mm});
            skArc(sketch, "E21.29.7", {"start": v(26.8, 14.5) * mm, "mid": v(28.37, 14.8) * mm, "end": v(29.97, 14.86) * mm});
            skArc(sketch, "E21.29.8", {"start": v(26.8, 14.5) * mm, "mid": v(26.3, 14.54) * mm, "end": v(25.9, 14.88) * mm});
            skLineSegment(sketch, "E21.29.9", {"start": v(25.9, 14.88) * mm, "end": v(25.88, 14.94) * mm});
            skArc(sketch, "E21.30.0", {"start": v(25.96, 15.97) * mm, "mid": v(25.74, 15.5) * mm, "end": v(25.84, 15) * mm});
            skLineSegment(sketch, "E21.30.1", {"start": v(25.84, 15) * mm, "end": v(25.88, 14.94) * mm});
            skArc(sketch, "E21.30.2", {"start": v(25.96, 15.97) * mm, "mid": v(27, 17.18) * mm, "end": v(27.86, 18.52) * mm});
            skArc(sketch, "E21.30.3", {"start": v(27.86, 18.52) * mm, "mid": v(27.95, 18.94) * mm, "end": v(27.82, 19.35) * mm});
            skLineSegment(sketch, "E21.30.4", {"start": v(27.82, 19.35) * mm, "end": v(27.76, 19.44) * mm});
            skLineSegment(sketch, "E21.30.5", {"start": v(27.7, 19.52) * mm, "end": v(27.76, 19.44) * mm});
            skArc(sketch, "E21.30.6", {"start": v(26.93, 19.84) * mm, "mid": v(27.36, 19.79) * mm, "end": v(27.7, 19.52) * mm});
            skArc(sketch, "E21.30.7", {"start": v(23.88, 18.94) * mm, "mid": v(25.37, 19.5) * mm, "end": v(26.93, 19.84) * mm});
            skArc(sketch, "E21.30.8", {"start": v(23.88, 18.94) * mm, "mid": v(23.37, 18.88) * mm, "end": v(22.93, 19.16) * mm});
            skLineSegment(sketch, "E21.30.9", {"start": v(22.93, 19.16) * mm, "end": v(22.89, 19.2) * mm});
            skArc(sketch, "E21.31.0", {"start": v(22.8, 20.23) * mm, "mid": v(22.65, 19.74) * mm, "end": v(22.85, 19.26) * mm});
            skLineSegment(sketch, "E21.31.1", {"start": v(22.85, 19.26) * mm, "end": v(22.89, 19.2) * mm});
            skArc(sketch, "E21.31.2", {"start": v(22.8, 20.23) * mm, "mid": v(23.6, 21.6) * mm, "end": v(24.22, 23.08) * mm});
            skArc(sketch, "E21.31.3", {"start": v(24.22, 23.08) * mm, "mid": v(24.24, 23.5) * mm, "end": v(24.03, 23.88) * mm});
            skLineSegment(sketch, "E21.31.4", {"start": v(24.03, 23.88) * mm, "end": v(23.96, 23.96) * mm});
            skLineSegment(sketch, "E21.31.5", {"start": v(23.88, 24.03) * mm, "end": v(23.96, 23.96) * mm});
            skArc(sketch, "E21.31.6", {"start": v(23.08, 24.22) * mm, "mid": v(23.5, 24.24) * mm, "end": v(23.88, 24.03) * mm});
            skArc(sketch, "E21.31.7", {"start": v(20.23, 22.8) * mm, "mid": v(21.6, 23.6) * mm, "end": v(23.08, 24.22) * mm});
            skArc(sketch, "E21.31.8", {"start": v(20.23, 22.8) * mm, "mid": v(19.74, 22.65) * mm, "end": v(19.26, 22.85) * mm});
            skLineSegment(sketch, "E21.31.9", {"start": v(19.26, 22.85) * mm, "end": v(19.2, 22.89) * mm});
            skArc(sketch, "E21.32.0", {"start": v(18.94, 23.88) * mm, "mid": v(18.88, 23.37) * mm, "end": v(19.16, 22.93) * mm});
            skLineSegment(sketch, "E21.32.1", {"start": v(19.16, 22.93) * mm, "end": v(19.2, 22.89) * mm});
            skArc(sketch, "E21.32.2", {"start": v(18.94, 23.88) * mm, "mid": v(19.5, 25.37) * mm, "end": v(19.84, 26.93) * mm});
            skArc(sketch, "E21.32.3", {"start": v(19.84, 26.93) * mm, "mid": v(19.79, 27.36) * mm, "end": v(19.52, 27.7) * mm});
            skLineSegment(sketch, "E21.32.4", {"start": v(19.52, 27.7) * mm, "end": v(19.44, 27.76) * mm});
            skLineSegment(sketch, "E21.32.5", {"start": v(19.35, 27.82) * mm, "end": v(19.44, 27.76) * mm});
            skArc(sketch, "E21.32.6", {"start": v(18.52, 27.86) * mm, "mid": v(18.94, 27.95) * mm, "end": v(19.35, 27.82) * mm});
            skArc(sketch, "E21.32.7", {"start": v(15.97, 25.96) * mm, "mid": v(17.18, 27) * mm, "end": v(18.52, 27.86) * mm});
            skArc(sketch, "E21.32.8", {"start": v(15.97, 25.96) * mm, "mid": v(15.5, 25.74) * mm, "end": v(15, 25.84) * mm});
            skLineSegment(sketch, "E21.32.9", {"start": v(15, 25.84) * mm, "end": v(14.94, 25.88) * mm});
            skArc(sketch, "E21.33.0", {"start": v(14.5, 26.8) * mm, "mid": v(14.54, 26.3) * mm, "end": v(14.88, 25.9) * mm});
            skLineSegment(sketch, "E21.33.1", {"start": v(14.88, 25.9) * mm, "end": v(14.94, 25.88) * mm});
            skArc(sketch, "E21.33.2", {"start": v(14.5, 26.8) * mm, "mid": v(14.8, 28.37) * mm, "end": v(14.86, 29.97) * mm});
            skArc(sketch, "E21.33.3", {"start": v(14.86, 29.97) * mm, "mid": v(14.74, 30.38) * mm, "end": v(14.41, 30.66) * mm});
            skLineSegment(sketch, "E21.33.4", {"start": v(14.41, 30.66) * mm, "end": v(14.32, 30.71) * mm});
            skLineSegment(sketch, "E21.33.5", {"start": v(14.22, 30.75) * mm, "end": v(14.32, 30.71) * mm});
            skArc(sketch, "E21.33.6", {"start": v(13.4, 30.65) * mm, "mid": v(13.8, 30.82) * mm, "end": v(14.22, 30.75) * mm});
            skArc(sketch, "E21.33.7", {"start": v(11.22, 28.34) * mm, "mid": v(12.23, 29.57) * mm, "end": v(13.4, 30.65) * mm});
            skArc(sketch, "E21.33.8", {"start": v(11.22, 28.34) * mm, "mid": v(10.8, 28.04) * mm, "end": v(10.28, 28.05) * mm});
            skLineSegment(sketch, "E21.33.9", {"start": v(10.28, 28.05) * mm, "end": v(10.22, 28.08) * mm});
            skArc(sketch, "E21.34.0", {"start": v(9.63, 28.92) * mm, "mid": v(9.75, 28.42) * mm, "end": v(10.16, 28.1) * mm});
            skLineSegment(sketch, "E21.34.1", {"start": v(10.16, 28.1) * mm, "end": v(10.22, 28.08) * mm});
            skArc(sketch, "E21.34.2", {"start": v(9.63, 28.92) * mm, "mid": v(9.64, 30.51) * mm, "end": v(9.43, 32.1) * mm});
            skArc(sketch, "E21.34.3", {"start": v(9.43, 32.1) * mm, "mid": v(9.24, 32.48) * mm, "end": v(8.87, 32.7) * mm});
            skLineSegment(sketch, "E21.34.4", {"start": v(8.87, 32.7) * mm, "end": v(8.77, 32.73) * mm});
            skLineSegment(sketch, "E21.34.5", {"start": v(8.67, 32.76) * mm, "end": v(8.77, 32.73) * mm});
            skArc(sketch, "E21.34.6", {"start": v(7.88, 32.51) * mm, "mid": v(8.24, 32.74) * mm, "end": v(8.67, 32.76) * mm});
            skArc(sketch, "E21.34.7", {"start": v(6.12, 29.86) * mm, "mid": v(6.9, 31.25) * mm, "end": v(7.88, 32.51) * mm});
            skArc(sketch, "E21.34.8", {"start": v(6.12, 29.86) * mm, "mid": v(5.76, 29.49) * mm, "end": v(5.25, 29.41) * mm});
            skLineSegment(sketch, "E21.34.9", {"start": v(5.25, 29.41) * mm, "end": v(5.19, 29.43) * mm});
            skArc(sketch, "E21.35.0", {"start": v(4.46, 30.15) * mm, "mid": v(4.67, 29.68) * mm, "end": v(5.12, 29.44) * mm});
            skLineSegment(sketch, "E21.35.1", {"start": v(5.12, 29.44) * mm, "end": v(5.19, 29.43) * mm});
            skArc(sketch, "E21.35.2", {"start": v(4.46, 30.15) * mm, "mid": v(4.2, 31.72) * mm, "end": v(3.72, 33.24) * mm});
            skArc(sketch, "E21.35.3", {"start": v(3.72, 33.24) * mm, "mid": v(3.46, 33.59) * mm, "end": v(3.06, 33.75) * mm});
            skLineSegment(sketch, "E21.35.4", {"start": v(3.06, 33.75) * mm, "end": v(2.95, 33.76) * mm});
            skLineSegment(sketch, "E21.35.5", {"start": v(2.85, 33.76) * mm, "end": v(2.95, 33.76) * mm});
            skArc(sketch, "E21.35.6", {"start": v(2.11, 33.38) * mm, "mid": v(2.43, 33.68) * mm, "end": v(2.85, 33.76) * mm});
            skArc(sketch, "E21.35.7", {"start": v(0.85, 30.47) * mm, "mid": v(1.38, 31.97) * mm, "end": v(2.11, 33.38) * mm});
            skArc(sketch, "E21.35.8", {"start": v(0.85, 30.47) * mm, "mid": v(0.56, 30.04) * mm, "end": v(0.07, 29.88) * mm});
            skLineSegment(sketch, "E21.35.9", {"start": v(0.07, 29.88) * mm, "end": v(0, 29.88) * mm});
            skSolve(sketch);
        }
        {
            var Q0;
            Q0=makeQuery(id+"F0.imprint","IMPRINT",FACE,{"disambiguationData":[TD([[makeQuery(id+"F0.imprint","IMPRINT",EDGE,{"derivedFrom":sQuery(id+"F0.wireOp",EDGE,"E8")}),1.0]])]});
            extrude(context, id + "F1", {"entities" : qUnion([Q0]), "depth" : 10 * mm});
        }
    });
